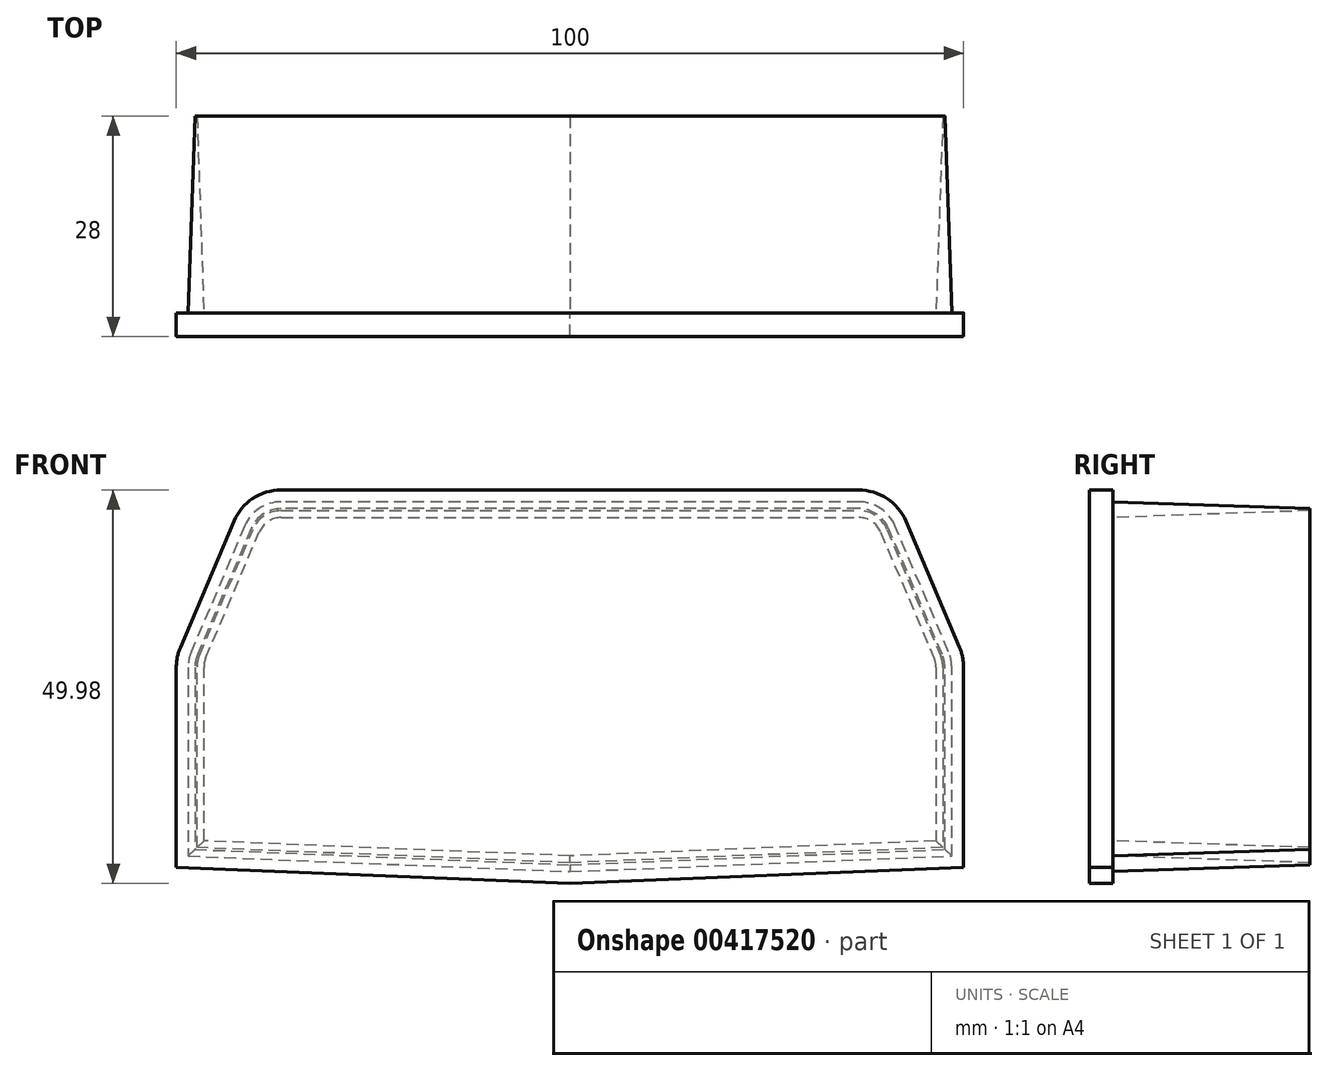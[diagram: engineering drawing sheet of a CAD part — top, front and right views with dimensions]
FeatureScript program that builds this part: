
annotation { "Feature Type Name" : "Feature", "Feature Type Description" : "" }
export const myFeature = defineFeature(function(context is Context, id is Id, definition is map)
    precondition{}
    {
        {
            var Q0;
            Q0=qCreatedBy(makeId("Front.planeOp"),FACE);
            var sketch = newSketch(context, id + "F0", { "sketchPlane" : qUnion([Q0])});
            skLineSegment(sketch, "E0.bottom", {"start": v(48.5, -12.5) * mm, "end": v(-48.5, -12.5) * mm});
            skLineSegment(sketch, "E0.top", {"start": v(48.5, 12.5) * mm, "end": v(-48.5, 12.5) * mm});
            skLineSegment(sketch, "E0.left", {"start": v(48.5, -12.5) * mm, "end": v(48.5, 11.48) * mm});
            skLineSegment(sketch, "E0.right", {"start": v(-48.5, -12.5) * mm, "end": v(-48.5, 11.48) * mm});
            skPoint(sketch, "E0.middle", {"position": v(0, 0) * mm});
            skLineSegment(sketch, "E1.bottom", {"start": v(-40, 12.5) * mm, "end": v(40, 12.5) * mm});
            skLineSegment(sketch, "E1.top", {"start": v(-36.7, 32.5) * mm, "end": v(36.7, 32.5) * mm});
            skLineSegment(sketch, "E1.left", {"start": v(-40, 12.5) * mm, "end": v(-40, 32.5) * mm});
            skLineSegment(sketch, "E1.right", {"start": v(40, 12.5) * mm, "end": v(40, 32.5) * mm});
            skLineSegment(sketch, "E2", {"start": v(0, 32.5) * mm, "end": v(0, -23.81) * mm});
            skLineSegment(sketch, "E3", {"start": v(41.3, 29.46) * mm, "end": v(48.1, 13.44) * mm});
            skLineSegment(sketch, "E4", {"start": v(-41.3, 29.46) * mm, "end": v(-48.1, 13.44) * mm});
            skLineSegment(sketch, "E5", {"start": v(-48.5, -12.5) * mm, "end": v(0, -14.48) * mm});
            skLineSegment(sketch, "E6", {"start": v(0, -14.48) * mm, "end": v(48.5, -12.5) * mm});
            skPoint(sketch, "E7.visualSharp", {"position": v(-40, 32.5) * mm});
            skArc(sketch, "E7.filletArc", {"start": v(-36.7, 32.5) * mm, "mid": v(-39.45, 31.67) * mm, "end": v(-41.3, 29.46) * mm});
            skPoint(sketch, "E8.visualSharp", {"position": v(-48.5, 12.5) * mm});
            skArc(sketch, "E8.filletArc", {"start": v(-48.1, 13.44) * mm, "mid": v(-48.4, 12.48) * mm, "end": v(-48.5, 11.48) * mm});
            skPoint(sketch, "E9.visualSharp", {"position": v(40, 32.5) * mm});
            skArc(sketch, "E9.filletArc", {"start": v(41.3, 29.46) * mm, "mid": v(39.45, 31.67) * mm, "end": v(36.7, 32.5) * mm});
            skPoint(sketch, "E10.visualSharp", {"position": v(48.5, 12.5) * mm});
            skArc(sketch, "E10.filletArc", {"start": v(48.5, 11.48) * mm, "mid": v(48.4, 12.48) * mm, "end": v(48.1, 13.44) * mm});
            skLineSegment(sketch, "E11.0", {"start": v(46.5, -10.58) * mm, "end": v(46.5, 11.48) * mm});
            skArc(sketch, "E11.1", {"start": v(46.5, 11.48) * mm, "mid": v(46.44, 12.08) * mm, "end": v(46.26, 12.66) * mm});
            skLineSegment(sketch, "E11.2", {"start": v(39.45, 28.67) * mm, "end": v(46.26, 12.66) * mm});
            skArc(sketch, "E11.3", {"start": v(39.45, 28.67) * mm, "mid": v(38.35, 30) * mm, "end": v(36.7, 30.5) * mm});
            skLineSegment(sketch, "E11.4", {"start": v(-36.7, 30.5) * mm, "end": v(36.7, 30.5) * mm});
            skLineSegment(sketch, "E11.5", {"start": v(0, -12.48) * mm, "end": v(46.5, -10.58) * mm});
            skLineSegment(sketch, "E11.6", {"start": v(-46.5, -10.58) * mm, "end": v(0, -12.48) * mm});
            skLineSegment(sketch, "E11.7", {"start": v(-46.5, -10.58) * mm, "end": v(-46.5, 11.48) * mm});
            skArc(sketch, "E11.8", {"start": v(-46.26, 12.66) * mm, "mid": v(-46.44, 12.08) * mm, "end": v(-46.5, 11.48) * mm});
            skLineSegment(sketch, "E11.9", {"start": v(-39.45, 28.67) * mm, "end": v(-46.26, 12.66) * mm});
            skArc(sketch, "E11.10", {"start": v(-36.7, 30.5) * mm, "mid": v(-38.35, 30) * mm, "end": v(-39.45, 28.67) * mm});
            skLineSegment(sketch, "E12.0", {"start": v(50, -13.94) * mm, "end": v(50, 11.48) * mm});
            skArc(sketch, "E12.1", {"start": v(50, 11.48) * mm, "mid": v(49.87, 12.78) * mm, "end": v(49.48, 14.02) * mm});
            skLineSegment(sketch, "E12.2", {"start": v(42.67, 30.04) * mm, "end": v(49.48, 14.02) * mm});
            skArc(sketch, "E12.3", {"start": v(42.67, 30.04) * mm, "mid": v(40.28, 32.92) * mm, "end": v(36.7, 34) * mm});
            skLineSegment(sketch, "E12.4", {"start": v(-36.7, 34) * mm, "end": v(36.7, 34) * mm});
            skLineSegment(sketch, "E12.5", {"start": v(0, -15.98) * mm, "end": v(50, -13.94) * mm});
            skLineSegment(sketch, "E12.6", {"start": v(-50, -13.94) * mm, "end": v(0, -15.98) * mm});
            skLineSegment(sketch, "E12.7", {"start": v(-50, -13.94) * mm, "end": v(-50, 11.48) * mm});
            skArc(sketch, "E12.8", {"start": v(-49.48, 14.02) * mm, "mid": v(-49.87, 12.78) * mm, "end": v(-50, 11.48) * mm});
            skLineSegment(sketch, "E12.9", {"start": v(-42.67, 30.04) * mm, "end": v(-49.48, 14.02) * mm});
            skArc(sketch, "E12.10", {"start": v(-36.7, 34) * mm, "mid": v(-40.28, 32.92) * mm, "end": v(-42.67, 30.04) * mm});
            skSolve(sketch);
        }
        {
            var Q0;
            {var subQ3=sQuery(id+"F0.wireOp",EDGE,"E11.8");var subQ5=sQuery(id+"F0.wireOp",EDGE,"E11.9");var subQ6=makeQuery(id+"F0.imprint","INTERSECT",VERTEX,{"derivedFrom":[subQ3,subQ5]});Q0=makeQuery(id+"F0.imprint","IMPRINT",FACE,{"disambiguationData":[TD([[makeQuery(id+"F0.imprint","IMPRINT",EDGE,{"disambiguationData":[TD([[subQ6,-1.0]])],"derivedFrom":subQ3}),1.0]])]});}
            var Q1;
            {var subQ11=sQuery(id+"F0.wireOp",EDGE,"E11.3");Q1=makeQuery(id+"F0.imprint","IMPRINT",FACE,{"disambiguationData":[TD([[makeQuery(id+"F0.imprint","IMPRINT",EDGE,{"derivedFrom":subQ11}),-1.0]])]});}
            var Q2;
            {var subQ4=sQuery(id+"F0.wireOp",EDGE,"E0.left");Q2=makeQuery(id+"F0.imprint","IMPRINT",FACE,{"disambiguationData":[TD([[makeQuery(id+"F0.imprint","IMPRINT",EDGE,{"derivedFrom":subQ4}),1.0]])]});}
            var Q3;
            {var subQ4=sQuery(id+"F0.wireOp",EDGE,"E0.right");Q3=makeQuery(id+"F0.imprint","IMPRINT",FACE,{"disambiguationData":[TD([[makeQuery(id+"F0.imprint","IMPRINT",EDGE,{"derivedFrom":subQ4}),-1.0]])]});}
            var Q4;
            {var subQ0=sQuery(id+"F0.wireOp",EDGE,"E11.10");Q4=makeQuery(id+"F0.imprint","IMPRINT",FACE,{"disambiguationData":[TD([[makeQuery(id+"F0.imprint","IMPRINT",EDGE,{"derivedFrom":subQ0}),1.0]])]});}
            var Q5;
            {var subQ3=sQuery(id+"F0.wireOp",EDGE,"E11.1");var subQ5=sQuery(id+"F0.wireOp",EDGE,"E11.2");var subQ7=makeQuery(id+"F0.imprint","INTERSECT",VERTEX,{"derivedFrom":[subQ3,subQ5]});Q5=makeQuery(id+"F0.imprint","IMPRINT",FACE,{"disambiguationData":[TD([[makeQuery(id+"F0.imprint","IMPRINT",EDGE,{"disambiguationData":[TD([[subQ7,1.0]])],"derivedFrom":subQ3}),1.0]])]});}
            var Q6;
            {var subQ0=sQuery(id+"F0.wireOp",EDGE,"E6");Q6=makeQuery(id+"F0.imprint","IMPRINT",FACE,{"disambiguationData":[TD([[makeQuery(id+"F0.imprint","IMPRINT",EDGE,{"derivedFrom":subQ0}),1.0]])]});}
            var Q7;
            {var subQ1=sQuery(id+"F0.wireOp",EDGE,"E4");Q7=makeQuery(id+"F0.imprint","IMPRINT",FACE,{"disambiguationData":[TD([[makeQuery(id+"F0.imprint","IMPRINT",EDGE,{"derivedFrom":subQ1}),1.0]])]});}
            var Q8;
            {var subQ5=sQuery(id+"F0.wireOp",EDGE,"E11.0");Q8=makeQuery(id+"F0.imprint","IMPRINT",FACE,{"disambiguationData":[TD([[makeQuery(id+"F0.imprint","IMPRINT",EDGE,{"derivedFrom":subQ5}),1.0]])]});}
            var Q9;
            {var subQ1=sQuery(id+"F0.wireOp",EDGE,"E3");Q9=makeQuery(id+"F0.imprint","IMPRINT",FACE,{"disambiguationData":[TD([[makeQuery(id+"F0.imprint","IMPRINT",EDGE,{"derivedFrom":subQ1}),-1.0]])]});}
            var Q10;
            {var subQ5=sQuery(id+"F0.wireOp",EDGE,"E0.left");Q10=makeQuery(id+"F0.imprint","IMPRINT",FACE,{"disambiguationData":[TD([[makeQuery(id+"F0.imprint","IMPRINT",EDGE,{"derivedFrom":subQ5}),-1.0]])]});}
            var Q11;
            {var subQ0=sQuery(id+"F0.wireOp",EDGE,"E5");Q11=makeQuery(id+"F0.imprint","IMPRINT",FACE,{"disambiguationData":[TD([[makeQuery(id+"F0.imprint","IMPRINT",EDGE,{"derivedFrom":subQ0}),1.0]])]});}
            var Q12;
            {var subQ0=sQuery(id+"F0.wireOp",EDGE,"E11.6");Q12=makeQuery(id+"F0.imprint","IMPRINT",FACE,{"disambiguationData":[TD([[makeQuery(id+"F0.imprint","IMPRINT",EDGE,{"derivedFrom":subQ0}),1.0]])]});}
            var Q13;
            {var subQ0=sQuery(id+"F0.wireOp",EDGE,"E11.3");Q13=makeQuery(id+"F0.imprint","IMPRINT",FACE,{"disambiguationData":[TD([[makeQuery(id+"F0.imprint","IMPRINT",EDGE,{"derivedFrom":subQ0}),1.0]])]});}
            var Q14;
            {var subQ10=sQuery(id+"F0.wireOp",EDGE,"E11.10");Q14=makeQuery(id+"F0.imprint","IMPRINT",FACE,{"disambiguationData":[TD([[makeQuery(id+"F0.imprint","IMPRINT",EDGE,{"derivedFrom":subQ10}),-1.0]])]});}
            extrude(context, id + "F1", {"entities" : qUnion([Q0, Q1, Q2, Q3, Q4, Q5, Q6, Q7, Q8, Q9, Q10, Q11, Q12, Q13, Q14]), "depth" : 3 * mm});
        }
        {
            var Q0;
            {var subQ10=sQuery(id+"F0.wireOp",EDGE,"E11.10");Q0=makeQuery(id+"F0.imprint","IMPRINT",FACE,{"disambiguationData":[TD([[makeQuery(id+"F0.imprint","IMPRINT",EDGE,{"derivedFrom":subQ10}),-1.0]])]});}
            var Q1;
            {var subQ1=sQuery(id+"F0.wireOp",EDGE,"E4");Q1=makeQuery(id+"F0.imprint","IMPRINT",FACE,{"disambiguationData":[TD([[makeQuery(id+"F0.imprint","IMPRINT",EDGE,{"derivedFrom":subQ1}),1.0]])]});}
            var Q2;
            {var subQ4=sQuery(id+"F0.wireOp",EDGE,"E0.right");Q2=makeQuery(id+"F0.imprint","IMPRINT",FACE,{"disambiguationData":[TD([[makeQuery(id+"F0.imprint","IMPRINT",EDGE,{"derivedFrom":subQ4}),-1.0]])]});}
            var Q3;
            {var subQ0=sQuery(id+"F0.wireOp",EDGE,"E5");Q3=makeQuery(id+"F0.imprint","IMPRINT",FACE,{"disambiguationData":[TD([[makeQuery(id+"F0.imprint","IMPRINT",EDGE,{"derivedFrom":subQ0}),1.0]])]});}
            var Q4;
            {var subQ0=sQuery(id+"F0.wireOp",EDGE,"E6");Q4=makeQuery(id+"F0.imprint","IMPRINT",FACE,{"disambiguationData":[TD([[makeQuery(id+"F0.imprint","IMPRINT",EDGE,{"derivedFrom":subQ0}),1.0]])]});}
            var Q5;
            {var subQ4=sQuery(id+"F0.wireOp",EDGE,"E0.left");Q5=makeQuery(id+"F0.imprint","IMPRINT",FACE,{"disambiguationData":[TD([[makeQuery(id+"F0.imprint","IMPRINT",EDGE,{"derivedFrom":subQ4}),1.0]])]});}
            var Q6;
            {var subQ1=sQuery(id+"F0.wireOp",EDGE,"E3");Q6=makeQuery(id+"F0.imprint","IMPRINT",FACE,{"disambiguationData":[TD([[makeQuery(id+"F0.imprint","IMPRINT",EDGE,{"derivedFrom":subQ1}),-1.0]])]});}
            var Q7;
            {var subQ11=sQuery(id+"F0.wireOp",EDGE,"E11.3");Q7=makeQuery(id+"F0.imprint","IMPRINT",FACE,{"disambiguationData":[TD([[makeQuery(id+"F0.imprint","IMPRINT",EDGE,{"derivedFrom":subQ11}),-1.0]])]});}
            extrude(context, id + "F2", {"entities" : qUnion([Q0, Q1, Q2, Q3, Q4, Q5, Q6, Q7]), "operationType" : NewBodyOperationType.ADD, "oppositeDirection" : true, "depth" : 25 * mm, "hasDraft" : true, "draftAngle" : 2 * degree, "draftPullDirection" : true});
        }
    });
